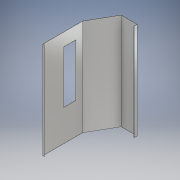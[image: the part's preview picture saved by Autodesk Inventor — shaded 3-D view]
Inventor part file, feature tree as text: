
AUTODESK INVENTOR PART (.ipt)
format: ipt  version: 2018 (Build 220112000, 112)  size: 136,704 bytes
history: native  units: mm
features: extrude x2, sketch x2, plane x1
ambient origin geometry x8: Origin, YZ Plane, XZ Plane, XY Plane, X Axis, Y Axis, Z Axis, Center Point
bodies: Solid1 (feature_tree)
feature tree (5):
  extrude  "main"  Depth=1200.0mm TaperAngle=0.0deg
  plane  "Work Plane1"
  extrude  "Extrusion4"  [1 undecoded]
  sketch  "Sketch1"  dims[d0=150.0deg d7=1200.0mm d8=0.0mm]
  sketch  "Sketch6"  dims[d25=25.5mm d26=0.0mm]
note: 1 required parameter value undecoded (feature->parameter linkage not recoverable at this tier; creation-order binding heuristic only, values carry confidence <= 0.55)
